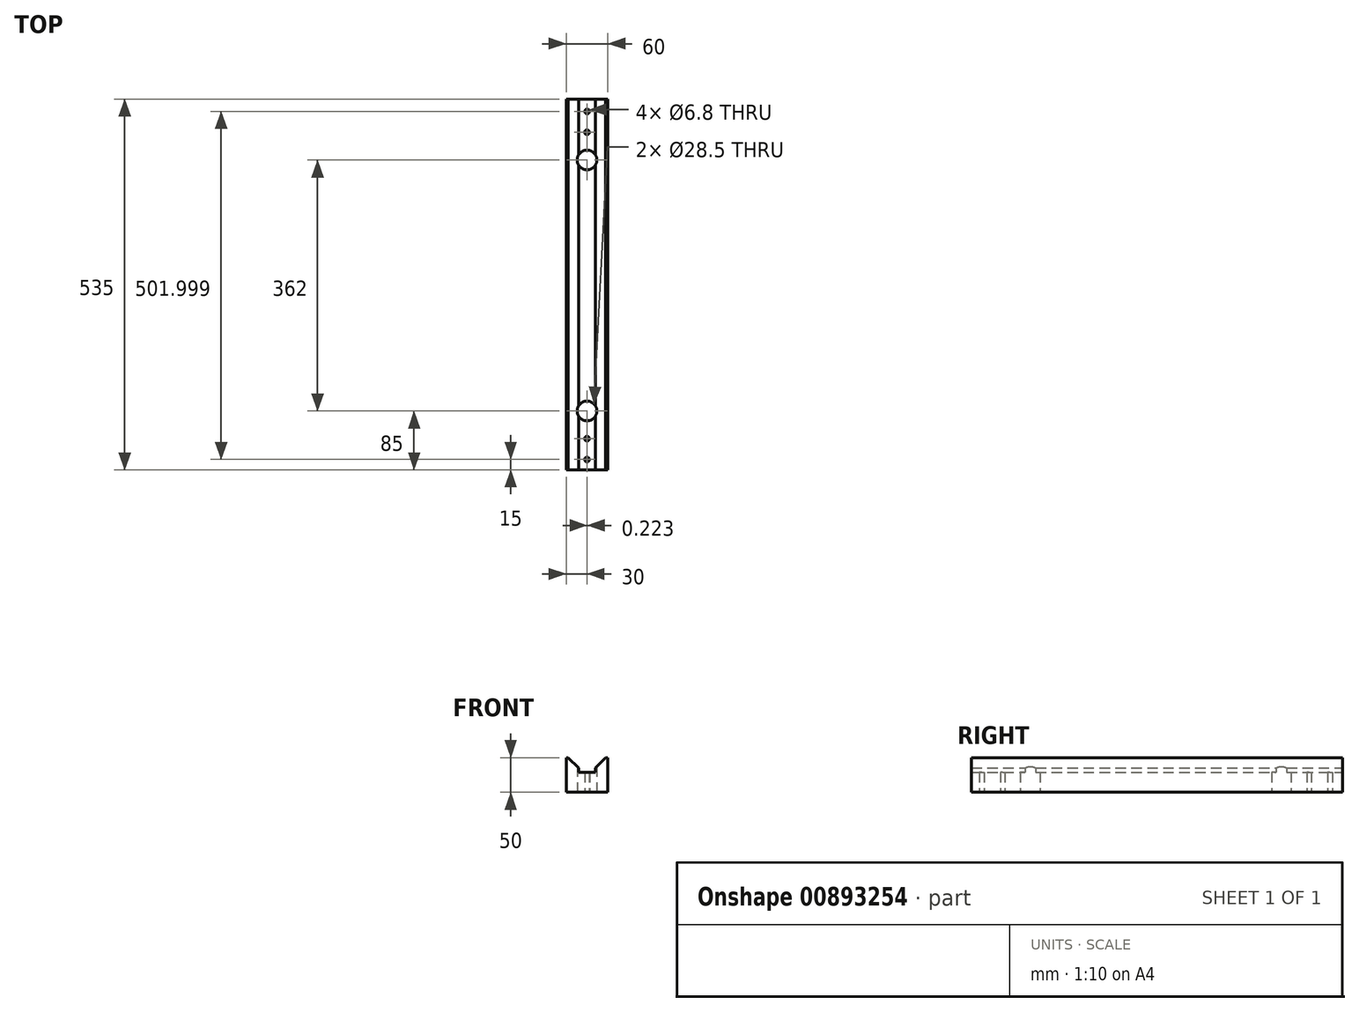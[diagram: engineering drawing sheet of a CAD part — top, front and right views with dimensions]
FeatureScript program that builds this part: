
annotation { "Feature Type Name" : "Feature", "Feature Type Description" : "" }
export const myFeature = defineFeature(function(context is Context, id is Id, definition is map)
    precondition{}
    {
        {
            var Q0;
            Q0=qCreatedBy(makeId("Front.planeOp"),FACE);
            var sketch = newSketch(context, id + "F0", { "sketchPlane" : qUnion([Q0])});
            skLineSegment(sketch, "E0", {"start": v(0, 0) * mm, "end": v(60, 0) * mm});
            skLineSegment(sketch, "E1", {"start": v(60, 0) * mm, "end": v(60, 50) * mm});
            skLineSegment(sketch, "E2", {"start": v(60, 50) * mm, "end": v(57, 50) * mm});
            skLineSegment(sketch, "E3", {"start": v(0, 0) * mm, "end": v(0, 50) * mm});
            skLineSegment(sketch, "E4", {"start": v(0, 50) * mm, "end": v(3, 50) * mm});
            skLineSegment(sketch, "E5", {"start": v(30, 29) * mm, "end": v(18, 29) * mm});
            skLineSegment(sketch, "E6", {"start": v(18, 29) * mm, "end": v(18, 35) * mm});
            skLineSegment(sketch, "E7", {"start": v(18, 35) * mm, "end": v(3, 50) * mm});
            skLineSegment(sketch, "E8.MirrorCS", {"start": v(42, 35) * mm, "end": v(57, 50) * mm});
            skLineSegment(sketch, "E9.MirrorCS", {"start": v(42, 29) * mm, "end": v(42, 35) * mm});
            skLineSegment(sketch, "E10.MirrorCS", {"start": v(30, 29) * mm, "end": v(42, 29) * mm});
            skSolve(sketch);
        }
        {
            var Q0;
            Q0=makeQuery(id+"F0.imprint","IMPRINT",FACE,{"disambiguationData":[TD([[makeQuery(id+"F0.imprint","IMPRINT",EDGE,{"derivedFrom":sQuery(id+"F0.wireOp",EDGE,"E0")}),1.0]])]});
            extrude(context, id + "F1", {"entities" : qUnion([Q0]), "depth" : 535 * mm, "offsetDistance" : 25 * mm});
        }
        {
            var Q0;
            Q0=makeQuery(id+"F1.opExtrude","SWEPT_FACE",FACE,{"disambiguationData":[OSD([sQuery(id+"F0.wireOp",EDGE,"E0")])]});
            var sketch = newSketch(context, id + "F2", { "sketchPlane" : qUnion([Q0])});
            skCircle(sketch, "E11", {"center": v(30, 520) * mm, "radius": 3.4 * mm});
            skCircle(sketch, "E12", {"center": v(30, 490) * mm, "radius": 3.4 * mm});
            skCircle(sketch, "E13", {"center": v(30, 450) * mm, "radius": 14.25 * mm});
            skCircle(sketch, "E14", {"center": v(30, 88) * mm, "radius": 14.25 * mm});
            skCircle(sketch, "E15", {"center": v(30, 48) * mm, "radius": 3.4 * mm});
            skCircle(sketch, "E16", {"center": v(30.22, 18) * mm, "radius": 3.4 * mm});
            skSolve(sketch);
        }
        {
            var Q0;
            Q0=makeQuery(id+"F2.imprint","IMPRINT",FACE,{"disambiguationData":[TD([[makeQuery(id+"F2.imprint","IMPRINT",EDGE,{"derivedFrom":sQuery(id+"F2.wireOp",EDGE,"E14")}),1.0]])]});
            var Q1;
            Q1=makeQuery(id+"F2.imprint","IMPRINT",FACE,{"disambiguationData":[TD([[makeQuery(id+"F2.imprint","IMPRINT",EDGE,{"derivedFrom":sQuery(id+"F2.wireOp",EDGE,"E15")}),1.0]])]});
            var Q2;
            Q2=makeQuery(id+"F2.imprint","IMPRINT",FACE,{"disambiguationData":[TD([[makeQuery(id+"F2.imprint","IMPRINT",EDGE,{"derivedFrom":sQuery(id+"F2.wireOp",EDGE,"E16")}),1.0]])]});
            var Q3;
            Q3=makeQuery(id+"F2.imprint","IMPRINT",FACE,{"disambiguationData":[TD([[makeQuery(id+"F2.imprint","IMPRINT",EDGE,{"derivedFrom":sQuery(id+"F2.wireOp",EDGE,"E13")}),1.0]])]});
            var Q4;
            Q4=makeQuery(id+"F2.imprint","IMPRINT",FACE,{"disambiguationData":[TD([[makeQuery(id+"F2.imprint","IMPRINT",EDGE,{"derivedFrom":sQuery(id+"F2.wireOp",EDGE,"E12")}),1.0]])]});
            var Q5;
            Q5=makeQuery(id+"F2.imprint","IMPRINT",FACE,{"disambiguationData":[TD([[makeQuery(id+"F2.imprint","IMPRINT",EDGE,{"derivedFrom":sQuery(id+"F2.wireOp",EDGE,"E11")}),1.0]])]});
            extrude(context, id + "F3", {"entities" : qUnion([Q0, Q1, Q2, Q3, Q4, Q5]), "operationType" : NewBodyOperationType.REMOVE, "oppositeDirection" : true, "depth" : 40 * mm, "offsetDistance" : 25 * mm});
        }
    });
